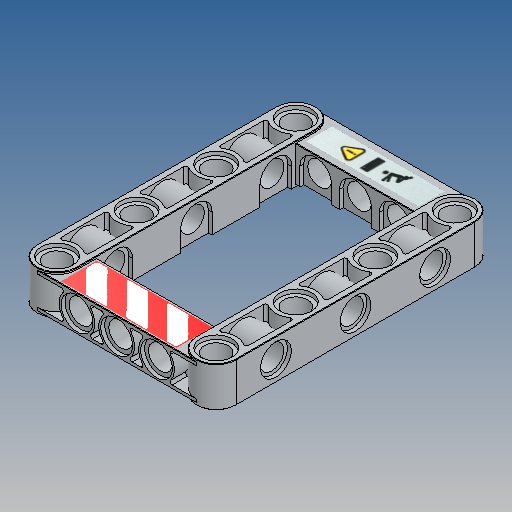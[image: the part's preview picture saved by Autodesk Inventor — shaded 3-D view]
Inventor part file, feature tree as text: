
AUTODESK INVENTOR PART (.ipt)
format: ipt  version: 2025 (Build 290162010, 162A)  size: 1,852,416 bytes
history: native  units: mm
features: extrude x13, sketch x11, other x4, mirror x3, fillet x2, projected_geometry x2, plane x1
ambient origin geometry x8: Origin, YZ Plane, XZ Plane, XY Plane, X Axis, Y Axis, Z Axis, Center Point
bodies: Solid1 (feature_tree)
feature tree (36):
  extrude  "Extrusion1"  Depth=0.8mm TaperAngle=0.0deg
  sketch  "Sketch6"  dims[d43=3.1mm d44=0.0mm d48=48.0mm]
  extrude  "Extrusion7"  Depth=3.1mm
  extrude  "Extrusion8"  Depth=4.8mm
  extrude  "Extrusion19"  Depth=0.4mm
  mirror  "Mirror5"
  sketch  "Sketch7"  dims[d49=6.4mm d50=4.8mm]
  extrude  "Extrusion9"  Depth=10.0mm
  extrude  "Extrusion10"  Depth=10.0mm TaperAngle=0.0deg
  extrude  "Extrusion11"  Depth=10.0mm
  extrude  "Extrusion18"  [1 undecoded]
  fillet  "Fillet2"  Radius=8.0mm
  plane  "Work Plane1"
  extrude  "Extrusion13"  Depth=5.8mm
  sketch  "Sketch12"  dims[d70=4.8mm d71=10.0mm d72=0.0mm]
  extrude  "Extrusion14"  Depth=0.9mm TaperAngle=0.0deg
  extrude  "Extrusion15"  Depth=0.4mm
  extrude  "Extrusion16"  Depth=0.4mm TaperAngle=0.0deg
  extrude  "Extrusion17"  Depth=0.4mm TaperAngle=0.0deg
  fillet  "Fillet3"  Radius=0.8mm
  mirror  "Mirror4"
  mirror  "Mirror3"
  other  "Aufkleber1"
  other  "Aufkleber2"
  projected_geometry  "Projected Loop4"
  sketch  "Skizze - Rechteckige Anordnung1"  dims[d14=8.0mm d15=0.0mm d41=0.8mm d42=0.0mm]
  sketch  "Sketch8"  dims[d51=16.0mm d60=0.4mm d61=0.1mm]
  sketch  "Sketch11"  dims[d62=30.0mm d64=16.0mm d65=10.0mm d67=10.0mm d69=7.2mm]
  projected_geometry  "Projected Loop5"
  sketch  "Sketch13"  dims[d73=10.0mm d74=0.0mm d75=6.2mm]
  sketch  "Sketch14"  dims[d76=0.8mm d77=0.0mm d78=-16.0mm d86=8.0mm]
  sketch  "Sketch15"  dims[d87=3.1mm d88=5.8mm]
  sketch  "Skizze16"  dims[d89=7.2mm d90=0.9mm d91=0.0mm]
  other  "Bild1"
  sketch  "Skizze17"  dims[d92=4.8mm d93=6.4mm d94=0.9mm d95=0.0mm d96=0.9mm d97=0.0mm d98=0.8mm d99=0.0mm d100=6.4mm d101=0.8mm d102=0.0mm d103=0.1mm d104=0.4mm d106=6.4mm d107=0.8mm d108=0.0mm d109=45.0deg d111=1.6mm d112=3.1mm d113=0.0mm d114=16.0mm d116=45.0deg d117=56.0mm d118=8.0mm d146=1.4mm d147=1.4mm d154=0.4mm d157=0.4mm]
  other  "Bild4"
note: 1 required parameter value undecoded (feature->parameter linkage not recoverable at this tier; creation-order binding heuristic only, values carry confidence <= 0.55)
